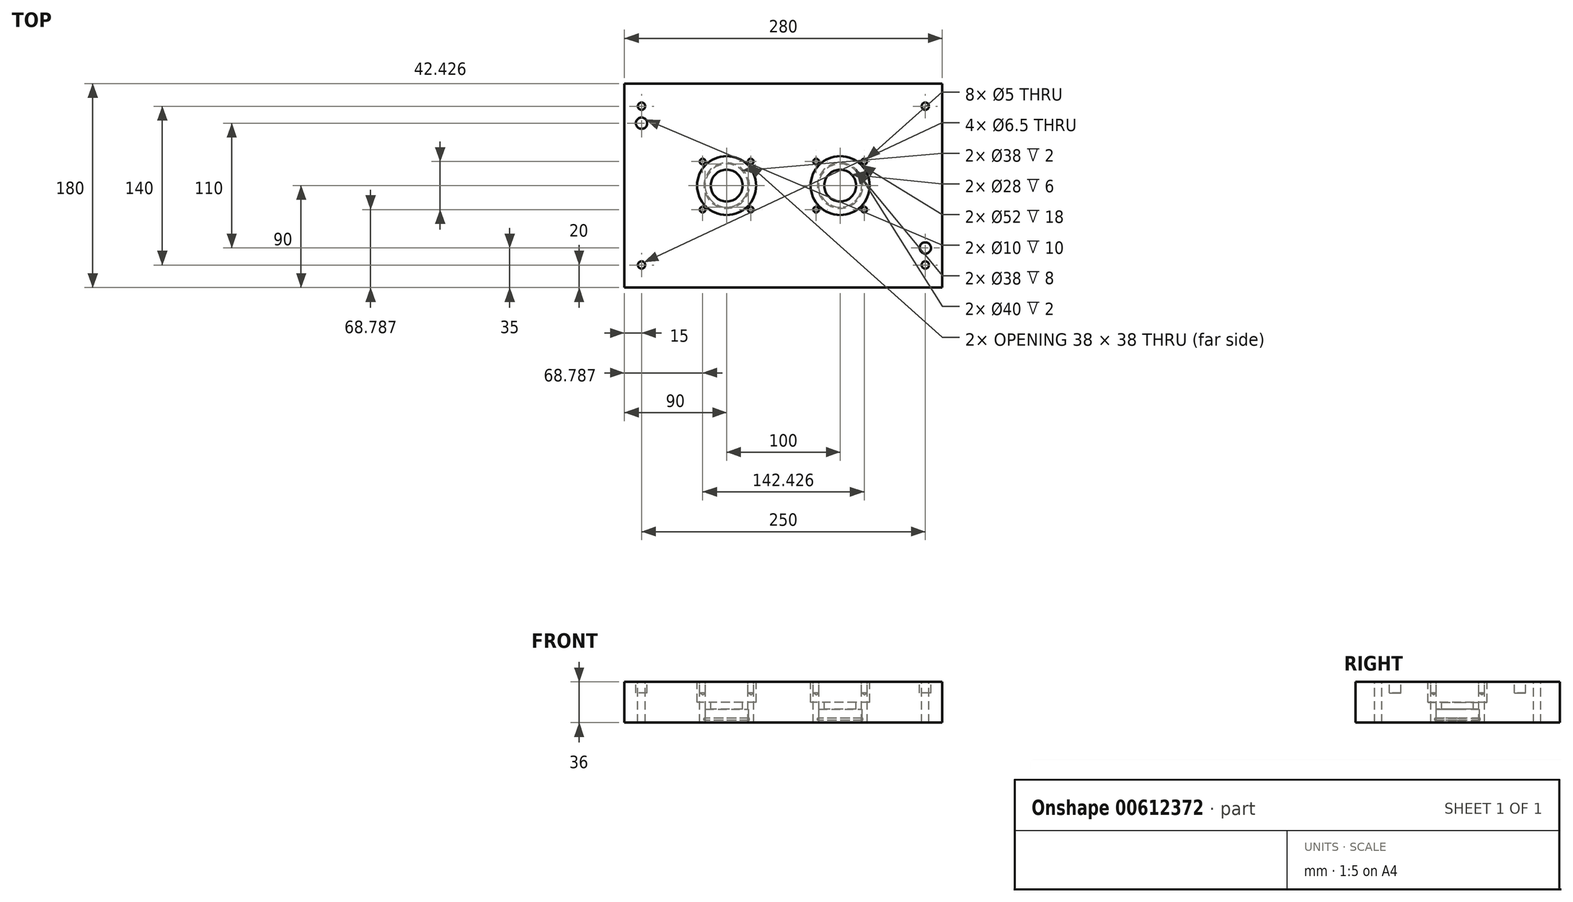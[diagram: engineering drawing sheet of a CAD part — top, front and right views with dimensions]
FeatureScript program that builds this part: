
annotation { "Feature Type Name" : "Feature", "Feature Type Description" : "" }
export const myFeature = defineFeature(function(context is Context, id is Id, definition is map)
    precondition{}
    {
        {
            var Q0;
            Q0=qCreatedBy(makeId("Top.planeOp"),FACE);
            var sketch = newSketch(context, id + "F0", { "sketchPlane" : qUnion([Q0])});
            skLineSegment(sketch, "E0.bottom", {"start": v(-140, 90) * mm, "end": v(140, 90) * mm});
            skLineSegment(sketch, "E0.top", {"start": v(-140, -90) * mm, "end": v(140, -90) * mm});
            skLineSegment(sketch, "E0.left", {"start": v(-140, 90) * mm, "end": v(-140, -90) * mm});
            skLineSegment(sketch, "E0.right", {"start": v(140, 90) * mm, "end": v(140, -90) * mm});
            skCircle(sketch, "E1", {"center": v(-50, 0) * mm, "radius": 26 * mm});
            skCircle(sketch, "E2", {"center": v(50, 0) * mm, "radius": 26 * mm});
            skCircle(sketch, "E3", {"center": v(-125, -70) * mm, "radius": 3.25 * mm});
            skCircle(sketch, "E4", {"center": v(125, -70) * mm, "radius": 3.25 * mm});
            skCircle(sketch, "E5", {"center": v(125, 70) * mm, "radius": 3.25 * mm});
            skCircle(sketch, "E6", {"center": v(-125, 70) * mm, "radius": 3.25 * mm});
            skCircle(sketch, "E7", {"center": v(-125, 55) * mm, "radius": 5 * mm});
            skCircle(sketch, "E8", {"center": v(125, -55) * mm, "radius": 5 * mm});
            skCircle(sketch, "E9", {"center": v(-50, 0) * mm, "radius": 14 * mm});
            skCircle(sketch, "E10", {"center": v(50, 0) * mm, "radius": 14 * mm});
            skCircle(sketch, "E11", {"center": v(-71.21, -21.21) * mm, "radius": 2.5 * mm});
            skCircle(sketch, "E12.MirrorC", {"center": v(-71.21, 21.21) * mm, "radius": 2.5 * mm});
            skCircle(sketch, "E13.MirrorC", {"center": v(-28.79, -21.21) * mm, "radius": 2.5 * mm});
            skCircle(sketch, "E14.MirrorC", {"center": v(-28.79, 21.21) * mm, "radius": 2.5 * mm});
            skCircle(sketch, "E15.MirrorC", {"center": v(28.79, 21.21) * mm, "radius": 2.5 * mm});
            skCircle(sketch, "E16.MirrorC", {"center": v(71.21, 21.21) * mm, "radius": 2.5 * mm});
            skCircle(sketch, "E17.MirrorC", {"center": v(28.79, -21.21) * mm, "radius": 2.5 * mm});
            skCircle(sketch, "E18.MirrorC", {"center": v(71.21, -21.21) * mm, "radius": 2.5 * mm});
            skSolve(sketch);
        }
        {
            var Q0;
            Q0=makeQuery(id+"F0.imprint","IMPRINT",FACE,{"disambiguationData":[TD([[makeQuery(id+"F0.imprint","IMPRINT",EDGE,{"derivedFrom":sQuery(id+"F0.wireOp",EDGE,"E0.bottom")}),-1.0]])]});
            var Q1;
            Q1=makeQuery(id+"F0.imprint","IMPRINT",FACE,{"disambiguationData":[TD([[makeQuery(id+"F0.imprint","IMPRINT",EDGE,{"derivedFrom":sQuery(id+"F0.wireOp",EDGE,"E1")}),1.0]])]});
            var Q2;
            Q2=makeQuery(id+"F0.imprint","IMPRINT",FACE,{"disambiguationData":[TD([[makeQuery(id+"F0.imprint","IMPRINT",EDGE,{"derivedFrom":sQuery(id+"F0.wireOp",EDGE,"E2")}),1.0]])]});
            var Q3;
            Q3=makeQuery(id+"F0.imprint","IMPRINT",FACE,{"disambiguationData":[TD([[makeQuery(id+"F0.imprint","IMPRINT",EDGE,{"derivedFrom":sQuery(id+"F0.wireOp",EDGE,"E7")}),1.0]])]});
            var Q4;
            Q4=makeQuery(id+"F0.imprint","IMPRINT",FACE,{"disambiguationData":[TD([[makeQuery(id+"F0.imprint","IMPRINT",EDGE,{"derivedFrom":sQuery(id+"F0.wireOp",EDGE,"E8")}),1.0]])]});
            var Q5;
            Q5=makeQuery(id+"F0.imprint","IMPRINT",FACE,{"disambiguationData":[TD([[makeQuery(id+"F0.imprint","IMPRINT",EDGE,{"derivedFrom":sQuery(id+"F0.wireOp",EDGE,"E12.MirrorC")}),-1.0]])]});
            var Q6;
            Q6=makeQuery(id+"F0.imprint","IMPRINT",FACE,{"disambiguationData":[TD([[makeQuery(id+"F0.imprint","IMPRINT",EDGE,{"derivedFrom":sQuery(id+"F0.wireOp",EDGE,"E11")}),1.0]])]});
            var Q7;
            Q7=makeQuery(id+"F0.imprint","IMPRINT",FACE,{"disambiguationData":[TD([[makeQuery(id+"F0.imprint","IMPRINT",EDGE,{"derivedFrom":sQuery(id+"F0.wireOp",EDGE,"E13.MirrorC")}),-1.0]])]});
            var Q8;
            Q8=makeQuery(id+"F0.imprint","IMPRINT",FACE,{"disambiguationData":[TD([[makeQuery(id+"F0.imprint","IMPRINT",EDGE,{"derivedFrom":sQuery(id+"F0.wireOp",EDGE,"E14.MirrorC")}),1.0]])]});
            var Q9;
            Q9=makeQuery(id+"F0.imprint","IMPRINT",FACE,{"disambiguationData":[TD([[makeQuery(id+"F0.imprint","IMPRINT",EDGE,{"derivedFrom":sQuery(id+"F0.wireOp",EDGE,"E15.MirrorC")}),-1.0]])]});
            var Q10;
            Q10=makeQuery(id+"F0.imprint","IMPRINT",FACE,{"disambiguationData":[TD([[makeQuery(id+"F0.imprint","IMPRINT",EDGE,{"derivedFrom":sQuery(id+"F0.wireOp",EDGE,"E17.MirrorC")}),1.0]])]});
            var Q11;
            Q11=makeQuery(id+"F0.imprint","IMPRINT",FACE,{"disambiguationData":[TD([[makeQuery(id+"F0.imprint","IMPRINT",EDGE,{"derivedFrom":sQuery(id+"F0.wireOp",EDGE,"E18.MirrorC")}),-1.0]])]});
            var Q12;
            Q12=makeQuery(id+"F0.imprint","IMPRINT",FACE,{"disambiguationData":[TD([[makeQuery(id+"F0.imprint","IMPRINT",EDGE,{"derivedFrom":sQuery(id+"F0.wireOp",EDGE,"E16.MirrorC")}),1.0]])]});
            extrude(context, id + "F1", {"entities" : qUnion([Q0, Q1, Q2, Q3, Q4, Q5, Q6, Q7, Q8, Q9, Q10, Q11, Q12]), "oppositeDirection" : true, "depth" : 36 * mm, "offsetDistance" : 25 * mm});
        }
        {
            var Q0;
            Q0=makeQuery(id+"F0.imprint","IMPRINT",FACE,{"disambiguationData":[TD([[makeQuery(id+"F0.imprint","IMPRINT",EDGE,{"derivedFrom":sQuery(id+"F0.wireOp",EDGE,"E1")}),1.0]])]});
            var Q1;
            Q1=makeQuery(id+"F0.imprint","IMPRINT",FACE,{"disambiguationData":[TD([[makeQuery(id+"F0.imprint","IMPRINT",EDGE,{"derivedFrom":sQuery(id+"F0.wireOp",EDGE,"E2")}),1.0]])]});
            extrude(context, id + "F2", {"entities" : qUnion([Q0, Q1]), "operationType" : NewBodyOperationType.REMOVE, "oppositeDirection" : true, "depth" : 18 * mm, "offsetDistance" : 25 * mm});
        }
        {
            var Q0;
            Q0=makeQuery(id+"F0.imprint","IMPRINT",FACE,{"disambiguationData":[TD([[makeQuery(id+"F0.imprint","IMPRINT",EDGE,{"derivedFrom":sQuery(id+"F0.wireOp",EDGE,"E7")}),1.0]])]});
            var Q1;
            Q1=makeQuery(id+"F0.imprint","IMPRINT",FACE,{"disambiguationData":[TD([[makeQuery(id+"F0.imprint","IMPRINT",EDGE,{"derivedFrom":sQuery(id+"F0.wireOp",EDGE,"E8")}),1.0]])]});
            extrude(context, id + "F3", {"entities" : qUnion([Q0, Q1]), "operationType" : NewBodyOperationType.REMOVE, "oppositeDirection" : true, "depth" : 10 * mm, "offsetDistance" : 25 * mm});
        }
        {
            var Q0;
            Q0=sQuery(id+"F0.wireOp",VERTEX,"E12.MirrorC.center");
            var Q1;
            Q1=sQuery(id+"F0.wireOp",VERTEX,"E11.center");
            var Q2;
            Q2=sQuery(id+"F0.wireOp",VERTEX,"E13.MirrorC.center");
            var Q3;
            Q3=sQuery(id+"F0.wireOp",VERTEX,"E14.MirrorC.center");
            var Q4;
            Q4=sQuery(id+"F0.wireOp",VERTEX,"E15.MirrorC.center");
            var Q5;
            Q5=sQuery(id+"F0.wireOp",VERTEX,"E17.MirrorC.center");
            var Q6;
            Q6=sQuery(id+"F0.wireOp",VERTEX,"E18.MirrorC.center");
            var Q7;
            Q7=sQuery(id+"F0.wireOp",VERTEX,"E16.MirrorC.center");
            var Q8;
            Q8=makeQuery(id+"F1.opExtrude","SWEPT_BODY",BODY,{"disambiguationData":[OSD([sQuery(id+"F0.wireOp",EDGE,"E0.bottom"),sQuery(id+"F0.wireOp",EDGE,"E0.top"),sQuery(id+"F0.wireOp",EDGE,"E0.left"),sQuery(id+"F0.wireOp",EDGE,"E0.right"),sQuery(id+"F0.wireOp",EDGE,"E3"),sQuery(id+"F0.wireOp",EDGE,"E4"),sQuery(id+"F0.wireOp",EDGE,"E5"),sQuery(id+"F0.wireOp",EDGE,"E6"),sQuery(id+"F0.wireOp",EDGE,"E9"),sQuery(id+"F0.wireOp",EDGE,"E10")])]});
            hole(context, id + "F4", {"style" : HoleStyle.SIMPLE, "endStyle" : HoleEndStyle.BLIND, "holeDiameter" : 5 * mm, "majorDiameter" : 5 * mm, "holeDepth" : 10 * mm, "isTappedThrough" : true, "tappedDepth" : 12 * mm, "tapClearance" : 3, "locations" : qUnion([Q0, Q1, Q2, Q3, Q4, Q5, Q6, Q7]), "scope" : qUnion([Q8])});
        }
        {
            var Q0;
            Q0=makeQuery(id+"F1.opExtrude","CAP_FACE",FACE,{"disambiguationData":[OSD([sQuery(id+"F0.wireOp",EDGE,"E0.bottom"),sQuery(id+"F0.wireOp",EDGE,"E0.top"),sQuery(id+"F0.wireOp",EDGE,"E0.left"),sQuery(id+"F0.wireOp",EDGE,"E0.right"),sQuery(id+"F0.wireOp",EDGE,"E3"),sQuery(id+"F0.wireOp",EDGE,"E4"),sQuery(id+"F0.wireOp",EDGE,"E5"),sQuery(id+"F0.wireOp",EDGE,"E6"),sQuery(id+"F0.wireOp",EDGE,"E9"),sQuery(id+"F0.wireOp",EDGE,"E10")])],"isStart":false});
            var sketch = newSketch(context, id + "F5", { "sketchPlane" : qUnion([Q0])});
            skCircle(sketch, "E19", {"center": v(50, 0) * mm, "radius": 19 * mm});
            skCircle(sketch, "E20", {"center": v(-50, 0) * mm, "radius": 19 * mm});
            skSolve(sketch);
        }
        {
            var Q0;
            Q0=makeQuery(id+"F5.imprint","IMPRINT",FACE,{"disambiguationData":[TD([[makeQuery(id+"F5.imprint","IMPRINT",EDGE,{"derivedFrom":sQuery(id+"F5.wireOp",EDGE,"E19")}),1.0]])]});
            var Q1;
            Q1=makeQuery(id+"F5.imprint","IMPRINT",FACE,{"disambiguationData":[TD([[makeQuery(id+"F5.imprint","IMPRINT",EDGE,{"derivedFrom":sQuery(id+"F5.wireOp",EDGE,"E20")}),1.0]])]});
            extrude(context, id + "F6", {"entities" : qUnion([Q0, Q1]), "operationType" : NewBodyOperationType.REMOVE, "oppositeDirection" : true, "depth" : 12 * mm, "offsetDistance" : 25 * mm});
        }
        {
            var Q0;
            Q0=qCreatedBy(makeId("Top.planeOp"),FACE);
            cPlane(context, id + "F7", {"entities" : qUnion([Q0]), "cplaneType" : CPlaneType.OFFSET, "offset" : 32 * mm, "oppositeDirection" : true, "width" : 150 * mm, "height" : 150 * mm});
        }
        {
            var Q0;
            Q0=qCreatedBy(id+"F7.planeOp",FACE);
            var sketch = newSketch(context, id + "F8", { "sketchPlane" : qUnion([Q0])});
            skCircle(sketch, "E21", {"center": v(-50, 0) * mm, "radius": 20 * mm});
            skCircle(sketch, "E22", {"center": v(50, 0) * mm, "radius": 20 * mm});
            skSolve(sketch);
        }
        {
            var Q0;
            Q0=makeQuery(id+"F8.imprint","IMPRINT",FACE,{"disambiguationData":[TD([[makeQuery(id+"F8.imprint","IMPRINT",EDGE,{"derivedFrom":sQuery(id+"F8.wireOp",EDGE,"E21")}),1.0]])]});
            var Q1;
            Q1=makeQuery(id+"F8.imprint","IMPRINT",FACE,{"disambiguationData":[TD([[makeQuery(id+"F8.imprint","IMPRINT",EDGE,{"derivedFrom":sQuery(id+"F8.wireOp",EDGE,"E22")}),1.0]])]});
            extrude(context, id + "F9", {"entities" : qUnion([Q0, Q1]), "operationType" : NewBodyOperationType.REMOVE, "oppositeDirection" : true, "depth" : 2 * mm, "offsetDistance" : 25 * mm});
        }
    });
